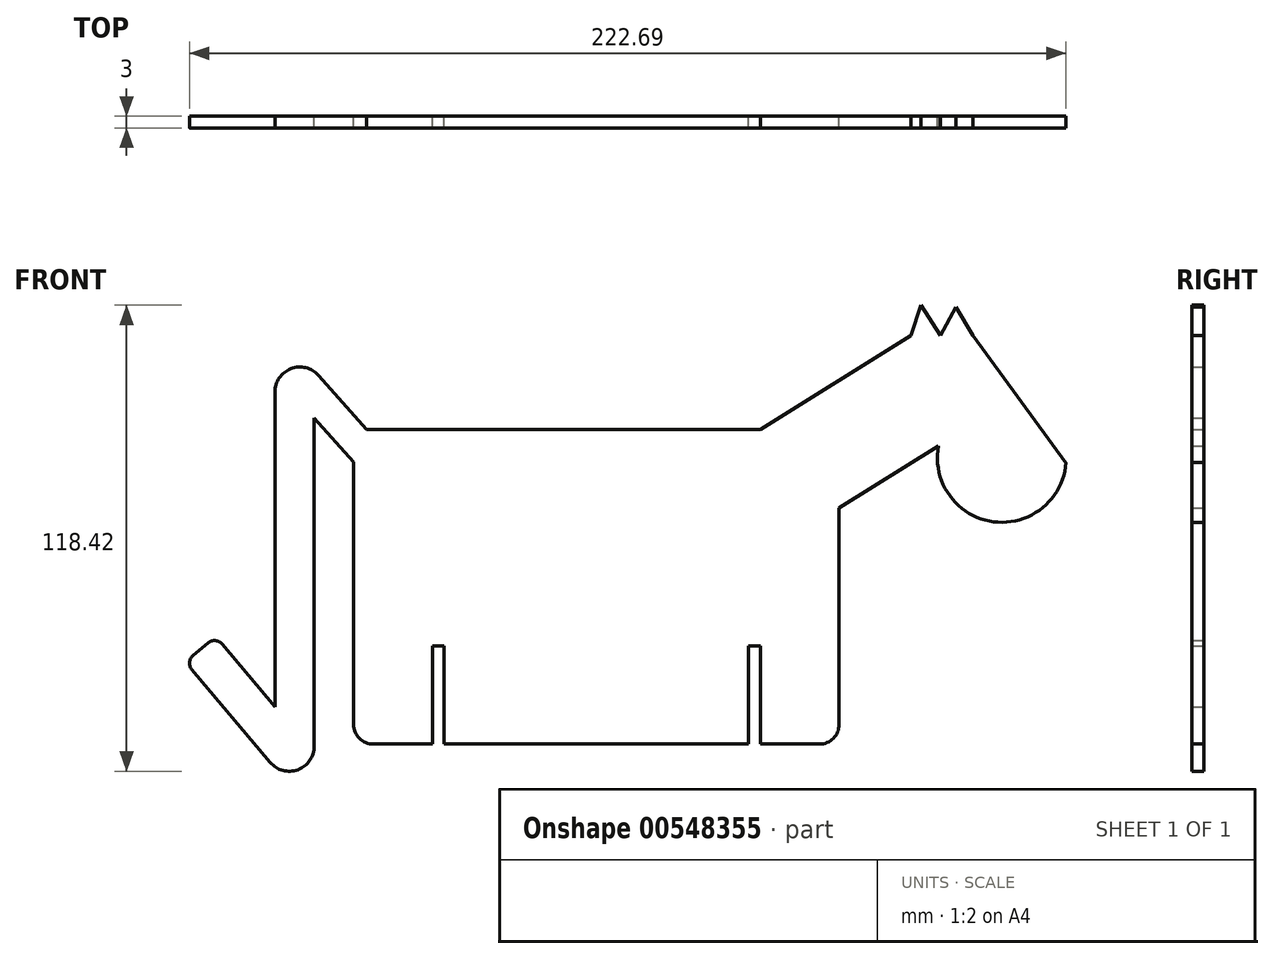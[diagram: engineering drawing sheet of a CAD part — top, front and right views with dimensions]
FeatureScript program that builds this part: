
annotation { "Feature Type Name" : "Feature", "Feature Type Description" : "" }
export const myFeature = defineFeature(function(context is Context, id is Id, definition is map)
    precondition{}
    {
        {
            var Q0;
            Q0=qCreatedBy(makeId("Front.planeOp"),FACE);
            var sketch = newSketch(context, id + "F0", { "sketchPlane" : qUnion([Q0])});
            skLineSegment(sketch, "E0.bottom", {"start": v(-5, 0) * mm, "end": v(-20, 0) * mm});
            skLineSegment(sketch, "E0.top", {"start": v(-20, 80) * mm, "end": v(-120, 80) * mm});
            skLineSegment(sketch, "E0.left", {"start": v(0, 5) * mm, "end": v(0, 60) * mm});
            skLineSegment(sketch, "E0.right", {"start": v(-123.33, 5) * mm, "end": v(-123.33, 71.73) * mm});
            skLineSegment(sketch, "E1", {"start": v(-20, 0) * mm, "end": v(-20, 25) * mm});
            skLineSegment(sketch, "E2", {"start": v(-20, 25) * mm, "end": v(-23, 25) * mm});
            skLineSegment(sketch, "E3", {"start": v(-23, 25) * mm, "end": v(-23, 0) * mm});
            skLineSegment(sketch, "E4", {"start": v(-118.33, 0) * mm, "end": v(-103.33, 0) * mm});
            skLineSegment(sketch, "E5", {"start": v(-103.33, 0) * mm, "end": v(-103.33, 25) * mm});
            skLineSegment(sketch, "E6", {"start": v(-103.33, 25) * mm, "end": v(-100.33, 25) * mm});
            skLineSegment(sketch, "E7", {"start": v(-100.33, 25) * mm, "end": v(-100.33, 0) * mm});
            skLineSegment(sketch, "E8", {"start": v(-20, 80) * mm, "end": v(18.2, 103.78) * mm});
            skLineSegment(sketch, "E9", {"start": v(0, 60) * mm, "end": v(25.24, 75.7) * mm});
            skLineSegment(sketch, "E10", {"start": v(18.2, 103.78) * mm, "end": v(20.82, 111.53) * mm});
            skLineSegment(sketch, "E11", {"start": v(20.82, 111.53) * mm, "end": v(25.76, 103.78) * mm});
            skLineSegment(sketch, "E12", {"start": v(25.76, 103.78) * mm, "end": v(29.7, 111.03) * mm});
            skLineSegment(sketch, "E13", {"start": v(29.7, 111.03) * mm, "end": v(33.98, 103.78) * mm});
            skLineSegment(sketch, "E14", {"start": v(33.98, 103.78) * mm, "end": v(57.58, 71.48) * mm});
            skArc(sketch, "E15", {"start": v(25.24, 75.7) * mm, "mid": v(39.26, 56.5) * mm, "end": v(57.67, 71.55) * mm});
            skPoint(sketch, "E16", {"position": v(57.58, 71.48) * mm});
            skLineSegment(sketch, "E17", {"start": v(57.58, 71.48) * mm, "end": v(57.67, 71.55) * mm});
            skLineSegment(sketch, "E18", {"start": v(57.58, 71.48) * mm, "end": v(57.58, 71.48) * mm});
            skLineSegment(sketch, "E19", {"start": v(-120, 80) * mm, "end": v(-132.25, 93.7) * mm});
            skLineSegment(sketch, "E20", {"start": v(-123.33, 71.73) * mm, "end": v(-133.33, 82.9) * mm});
            skLineSegment(sketch, "E21", {"start": v(-143.33, 89.46) * mm, "end": v(-143.33, 9.46) * mm});
            skLineSegment(sketch, "E22.trimOffspring", {"start": v(-23, 0) * mm, "end": v(-100.33, 0) * mm});
            skLineSegment(sketch, "E23.trimOffspring", {"start": v(-103.33, 0) * mm, "end": v(-118.33, 0) * mm});
            skLineSegment(sketch, "E24", {"start": v(-143.33, 9.46) * mm, "end": v(-156.79, 25.44) * mm});
            skLineSegment(sketch, "E25", {"start": v(-160.28, 25.74) * mm, "end": v(-164.14, 22.49) * mm});
            skArc(sketch, "E26.filletArc", {"start": v(-132.25, 93.7) * mm, "mid": v(-139.25, 95.4) * mm, "end": v(-143.33, 89.46) * mm});
            skArc(sketch, "E27.filletArc", {"start": v(-156.79, 25.44) * mm, "mid": v(-158.47, 26.31) * mm, "end": v(-160.28, 25.74) * mm});
            skPoint(sketch, "E28.visualSharp", {"position": v(-161.23, 24.94) * mm});
            skArc(sketch, "E28.filletArc", {"start": v(-164.14, 22.49) * mm, "mid": v(-165, 20.8) * mm, "end": v(-164.44, 19) * mm});
            skLineSegment(sketch, "E29", {"start": v(-133.33, 82.9) * mm, "end": v(-133.33, -0.54) * mm});
            skLineSegment(sketch, "E30", {"start": v(-144.54, -4.63) * mm, "end": v(-164.44, 19) * mm});
            skArc(sketch, "E31.filletArc", {"start": v(-5, 0) * mm, "mid": v(-1.46, 1.46) * mm, "end": v(0, 5) * mm});
            skArc(sketch, "E32.filletArc", {"start": v(-123.33, 5) * mm, "mid": v(-121.87, 1.46) * mm, "end": v(-118.33, 0) * mm});
            skPoint(sketch, "E33.visualSharp", {"position": v(-133.33, -17.93) * mm});
            skArc(sketch, "E33.filletArc", {"start": v(-144.54, -4.63) * mm, "mid": v(-137.5, -6.5) * mm, "end": v(-133.33, -0.54) * mm});
            skSolve(sketch);
        }
        {
            var Q0;
            Q0=makeQuery(id+"F0.imprint","IMPRINT",FACE,{"disambiguationData":[TD([[makeQuery(id+"F0.imprint","IMPRINT",EDGE,{"derivedFrom":sQuery(id+"F0.wireOp",EDGE,"E0.top")}),1.0]])]});
            extrude(context, id + "F1", {"entities" : qUnion([Q0]), "depth" : 3 * mm});
        }
    });
